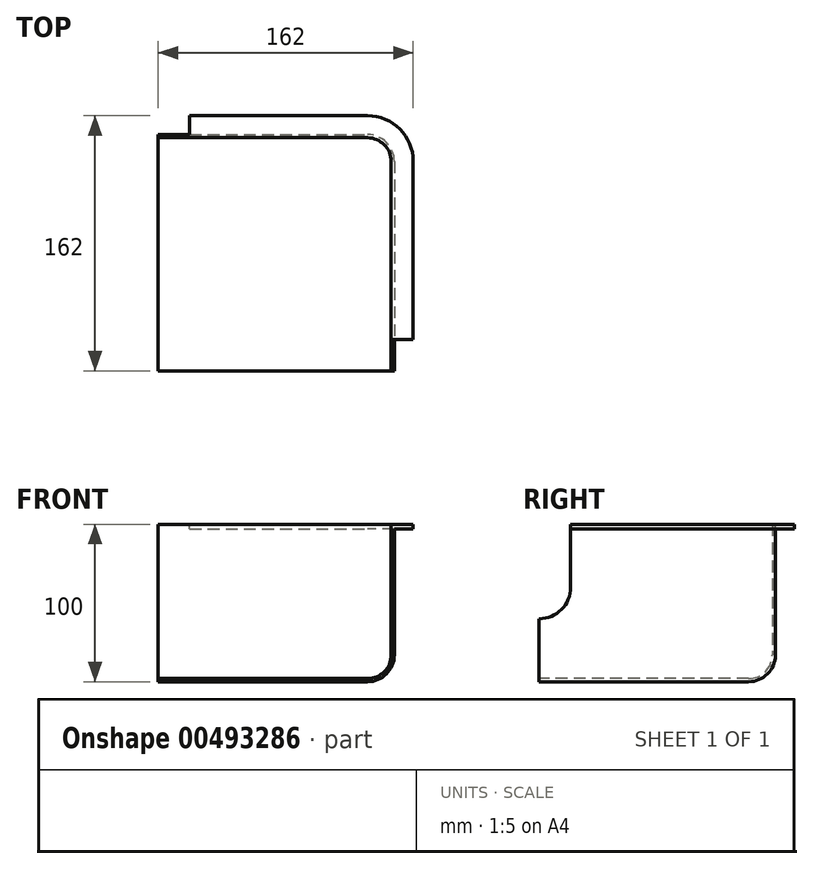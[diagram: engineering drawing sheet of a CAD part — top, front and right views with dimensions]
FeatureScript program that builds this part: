
annotation { "Feature Type Name" : "Feature", "Feature Type Description" : "" }
export const myFeature = defineFeature(function(context is Context, id is Id, definition is map)
    precondition{}
    {
        {
            var Q0;
            Q0=qCreatedBy(makeId("Top.planeOp"),FACE);
            var sketch = newSketch(context, id + "F0", { "sketchPlane" : qUnion([Q0])});
            skLineSegment(sketch, "E0", {"start": v(-150, 0) * mm, "end": v(0, 0) * mm});
            skLineSegment(sketch, "E1", {"start": v(0, 0) * mm, "end": v(0, -150) * mm});
            skLineSegment(sketch, "E2", {"start": v(0, -150) * mm, "end": v(-2, -150) * mm});
            skLineSegment(sketch, "E3", {"start": v(-150, 0) * mm, "end": v(-150, -2) * mm});
            skLineSegment(sketch, "E4", {"start": v(-150, -2) * mm, "end": v(-2, -2) * mm});
            skLineSegment(sketch, "E5", {"start": v(-2, -2) * mm, "end": v(-2, -150) * mm});
            skSolve(sketch);
        }
        {
            var Q0;
            Q0 = qSketchRegion(id + "F0", true);
            extrude(context, id + "F1", {"entities" : qUnion([Q0]), "depth" : 100 * mm});
        }
        {
            var Q0;
            Q0=makeQuery(id+"F1.opExtrude","CAP_FACE",FACE,{"disambiguationData":[OSD([sQuery(id+"F0.wireOp",EDGE,"E0"),sQuery(id+"F0.wireOp",EDGE,"E1"),sQuery(id+"F0.wireOp",EDGE,"E2"),sQuery(id+"F0.wireOp",EDGE,"E3"),sQuery(id+"F0.wireOp",EDGE,"E4"),sQuery(id+"F0.wireOp",EDGE,"E5")])],"isStart":true});
            var sketch = newSketch(context, id + "F2", { "sketchPlane" : qUnion([Q0])});
            skPoint(sketch, "E6.oppositeSnap0", {"position": v(-1, 150) * mm});
            skLineSegment(sketch, "E6.bottom", {"start": v(0, 0) * mm, "end": v(-150, 0) * mm});
            skLineSegment(sketch, "E6.top", {"start": v(0, 150) * mm, "end": v(-150, 150) * mm});
            skLineSegment(sketch, "E6.left", {"start": v(0, 0) * mm, "end": v(0, 150) * mm});
            skLineSegment(sketch, "E6.right", {"start": v(-150, 0) * mm, "end": v(-150, 150) * mm});
            skSolve(sketch);
        }
        {
            var Q0;
            Q0 = qSketchRegion(id + "F2", true);
            extrude(context, id + "F3", {"entities" : qUnion([Q0]), "operationType" : NewBodyOperationType.ADD, "oppositeDirection" : true, "depth" : 2 * mm});
        }
        {
            var Q0;
            Q0=makeQuery(id+"F3.boolean.opBoolean","INTERSECT",EDGE,{"derivedFrom":[makeQuery(id+"F1.opExtrude","SWEPT_FACE",FACE,{"disambiguationData":[OSD([sQuery(id+"F0.wireOp",EDGE,"E5")])]}),makeQuery(id+"F3.opExtrude","CAP_FACE",FACE,{"disambiguationData":[OSD([sQuery(id+"F2.wireOp",EDGE,"E6.bottom"),sQuery(id+"F2.wireOp",EDGE,"E6.top"),sQuery(id+"F2.wireOp",EDGE,"E6.left"),sQuery(id+"F2.wireOp",EDGE,"E6.right")])],"isStart":false})]});
            var Q1;
            Q1=makeQuery(id+"F3.boolean.opBoolean","INTERSECT",EDGE,{"derivedFrom":[makeQuery(id+"F1.opExtrude","SWEPT_FACE",FACE,{"disambiguationData":[OSD([sQuery(id+"F0.wireOp",EDGE,"E4")])]}),makeQuery(id+"F3.opExtrude","CAP_FACE",FACE,{"disambiguationData":[OSD([sQuery(id+"F2.wireOp",EDGE,"E6.bottom"),sQuery(id+"F2.wireOp",EDGE,"E6.top"),sQuery(id+"F2.wireOp",EDGE,"E6.left"),sQuery(id+"F2.wireOp",EDGE,"E6.right")])],"isStart":false})]});
            var Q2;
            Q2=makeQuery(id+"F1.opExtrude","SWEPT_EDGE",EDGE,{"disambiguationData":[OSD([sQuery(id+"F0.wireOp",EDGE,"E4"),sQuery(id+"F0.wireOp",EDGE,"E5")])]});
            fillet(context, id + "F4", {"entities" : qUnion([Q0, Q1, Q2]), "radius" : 15 * mm, "tangentPropagation" : true, "allowEdgeOverflow" : false});
        }
        {
            var Q0;
            Q0=makeQuery(id+"F1.opExtrude","CAP_EDGE",EDGE,{"disambiguationData":[OSD([sQuery(id+"F0.wireOp",EDGE,"E1")])],"isStart":true});
            var Q1;
            Q1=makeQuery(id+"F1.opExtrude","CAP_EDGE",EDGE,{"disambiguationData":[OSD([sQuery(id+"F0.wireOp",EDGE,"E0")])],"isStart":true});
            var Q2;
            Q2=makeQuery(id+"F1.opExtrude","SWEPT_EDGE",EDGE,{"disambiguationData":[OSD([sQuery(id+"F0.wireOp",EDGE,"E0"),sQuery(id+"F0.wireOp",EDGE,"E1")])]});
            fillet(context, id + "F5", {"entities" : qUnion([Q0, Q1, Q2]), "radius" : 17 * mm, "tangentPropagation" : true, "allowEdgeOverflow" : false});
        }
        {
            var Q0;
            Q0=makeQuery(id+"F1.opExtrude","SWEPT_FACE",FACE,{"disambiguationData":[OSD([sQuery(id+"F0.wireOp",EDGE,"E1")])]});
            var sketch = newSketch(context, id + "F6", { "sketchPlane" : qUnion([Q0])});
            skArc(sketch, "E7", {"start": v(-150, 40) * mm, "mid": v(-135.86, 45.86) * mm, "end": v(-130, 60) * mm});
            skLineSegment(sketch, "E8", {"start": v(-130, 60) * mm, "end": v(-130, 100) * mm});
            skLineSegment(sketch, "E9", {"start": v(-150, 40) * mm, "end": v(-150, 100) * mm});
            skLineSegment(sketch, "E10", {"start": v(-150, 100) * mm, "end": v(-130, 100) * mm});
            skSolve(sketch);
        }
        {
            var Q0;
            Q0 = qSketchRegion(id + "F6", true);
            extrude(context, id + "F7", {"entities" : qUnion([Q0]), "operationType" : NewBodyOperationType.REMOVE, "endBound" : BoundingType.THROUGH_ALL, "oppositeDirection" : true, "depth" : 25 * mm});
        }
        {
            var Q0;
            Q0=makeQuery(id+"F3.boolean.opBoolean","MERGE",FACE,{"derivedFrom":[makeQuery(id+"F1.opExtrude","SWEPT_FACE",FACE,{"disambiguationData":[OSD([sQuery(id+"F0.wireOp",EDGE,"E2")])]}),makeQuery(id+"F3.opExtrude","SWEPT_FACE",FACE,{"disambiguationData":[OSD([sQuery(id+"F2.wireOp",EDGE,"E6.top")])]})]});
            var sketch = newSketch(context, id + "F8", { "sketchPlane" : qUnion([Q0])});
            skLineSegment(sketch, "E11", {"start": v(-150, 0) * mm, "end": v(-150, 26.8) * mm, "construction": true});
            skSolve(sketch);
        }
        {
            var Q0;
            Q0=makeQuery(id+"F1.opExtrude","CAP_FACE",FACE,{"disambiguationData":[OSD([sQuery(id+"F0.wireOp",EDGE,"E0"),sQuery(id+"F0.wireOp",EDGE,"E1"),sQuery(id+"F0.wireOp",EDGE,"E2"),sQuery(id+"F0.wireOp",EDGE,"E3"),sQuery(id+"F0.wireOp",EDGE,"E4"),sQuery(id+"F0.wireOp",EDGE,"E5")])],"isStart":false});
            var sketch = newSketch(context, id + "F9", { "sketchPlane" : qUnion([Q0])});
            skLineSegment(sketch, "E12", {"start": v(-130, 0) * mm, "end": v(-130, 12) * mm});
            skLineSegment(sketch, "E13.0", {"start": v(-130, 12) * mm, "end": v(-17, 12) * mm});
            skArc(sketch, "E13.1", {"start": v(12, -17) * mm, "mid": v(3.5, 3.5) * mm, "end": v(-17, 12) * mm});
            skLineSegment(sketch, "E14", {"start": v(-2, -130) * mm, "end": v(12, -130) * mm});
            skLineSegment(sketch, "E15", {"start": v(12, -17) * mm, "end": v(12, -130) * mm});
            skLineSegment(sketch, "E16.0", {"start": v(-130, 0) * mm, "end": v(-17, 0) * mm});
            skArc(sketch, "E16.1", {"start": v(0, -17) * mm, "mid": v(-4.98, -4.98) * mm, "end": v(-17, 0) * mm});
            skLineSegment(sketch, "E16.2", {"start": v(0, -17) * mm, "end": v(0, -130) * mm});
            skSolve(sketch);
        }
        {
            var Q0;
            Q0 = qSketchRegion(id + "F9", true);
            extrude(context, id + "F10", {"entities" : qUnion([Q0]), "operationType" : NewBodyOperationType.ADD, "oppositeDirection" : true, "depth" : 3 * mm});
        }
    });
